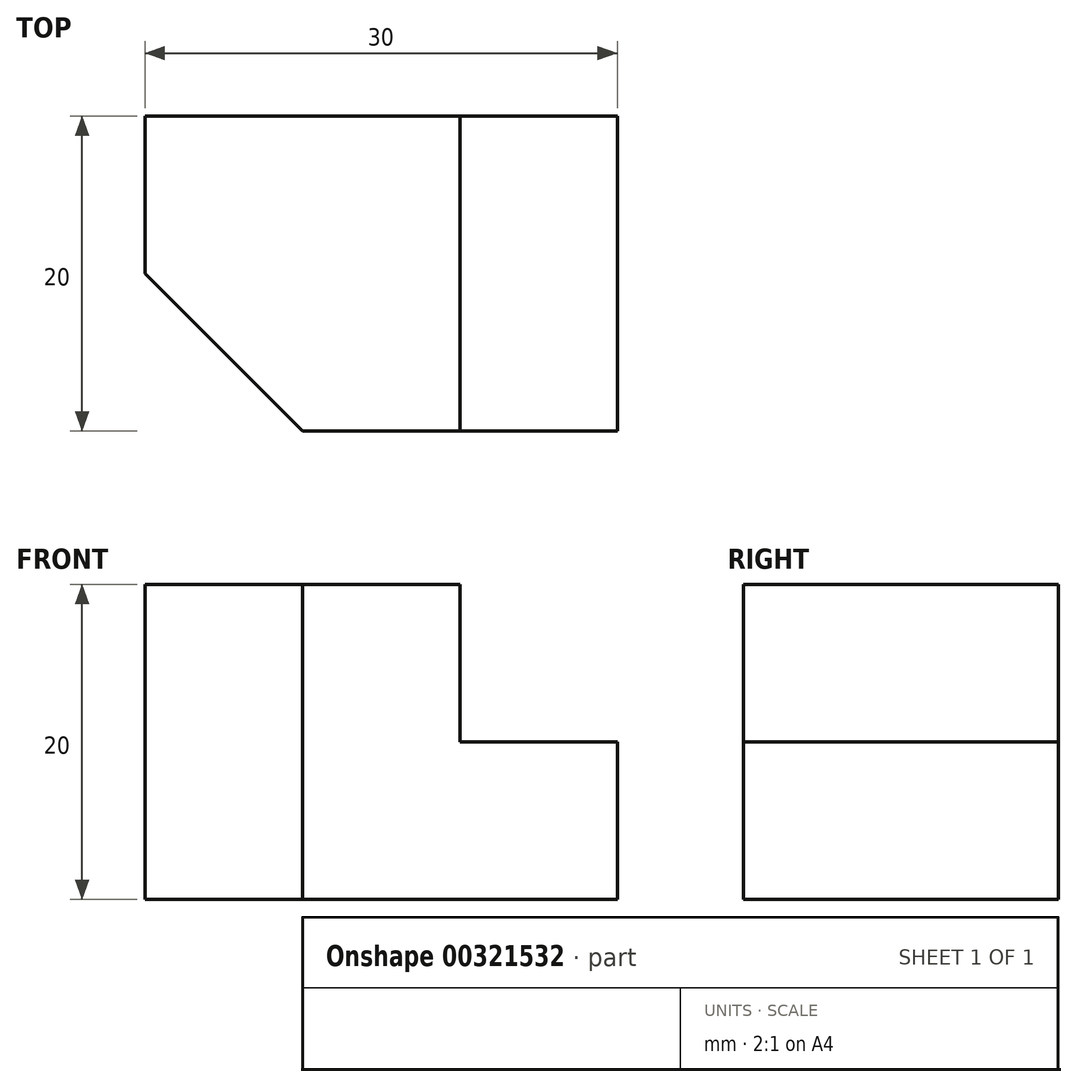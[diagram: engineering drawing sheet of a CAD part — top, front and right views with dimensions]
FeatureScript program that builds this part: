
annotation { "Feature Type Name" : "Feature", "Feature Type Description" : "" }
export const myFeature = defineFeature(function(context is Context, id is Id, definition is map)
    precondition{}
    {
        {
            var Q0;
            Q0=qCreatedBy(makeId("Top.planeOp"),FACE);
            var sketch = newSketch(context, id + "F0", { "sketchPlane" : qUnion([Q0])});
            skLineSegment(sketch, "E0", {"start": v(0, 10) * mm, "end": v(0, 20) * mm});
            skLineSegment(sketch, "E1", {"start": v(0, 20) * mm, "end": v(30, 20) * mm});
            skLineSegment(sketch, "E2", {"start": v(30, 20) * mm, "end": v(30, 0) * mm});
            skLineSegment(sketch, "E3", {"start": v(30, 0) * mm, "end": v(20, 0) * mm});
            skLineSegment(sketch, "E4", {"start": v(20, 0) * mm, "end": v(20, 20) * mm});
            skLineSegment(sketch, "E5", {"start": v(20, 20) * mm, "end": v(20, 0) * mm});
            skLineSegment(sketch, "E6", {"start": v(0, 10) * mm, "end": v(10, 0) * mm});
            skLineSegment(sketch, "E7", {"start": v(10, 0) * mm, "end": v(20, 0) * mm});
            skSolve(sketch);
        }
        {
            var Q0;
            {var subQ1=sQuery(id+"F0.wireOp",EDGE,"E0");Q0=makeQuery(id+"F0.imprint","IMPRINT",FACE,{"disambiguationData":[TD([[makeQuery(id+"F0.imprint","IMPRINT",EDGE,{"derivedFrom":subQ1}),-1.0]])]});}
            extrude(context, id + "F1", {"entities" : qUnion([Q0]), "depth" : 20 * mm});
        }
        {
            var Q0;
            {var subQ0=sQuery(id+"F0.wireOp",EDGE,"E2");Q0=makeQuery(id+"F0.imprint","IMPRINT",FACE,{"disambiguationData":[TD([[makeQuery(id+"F0.imprint","IMPRINT",EDGE,{"derivedFrom":subQ0}),-1.0]])]});}
            extrude(context, id + "F2", {"entities" : qUnion([Q0]), "operationType" : NewBodyOperationType.ADD, "depth" : 10 * mm});
        }
    });
